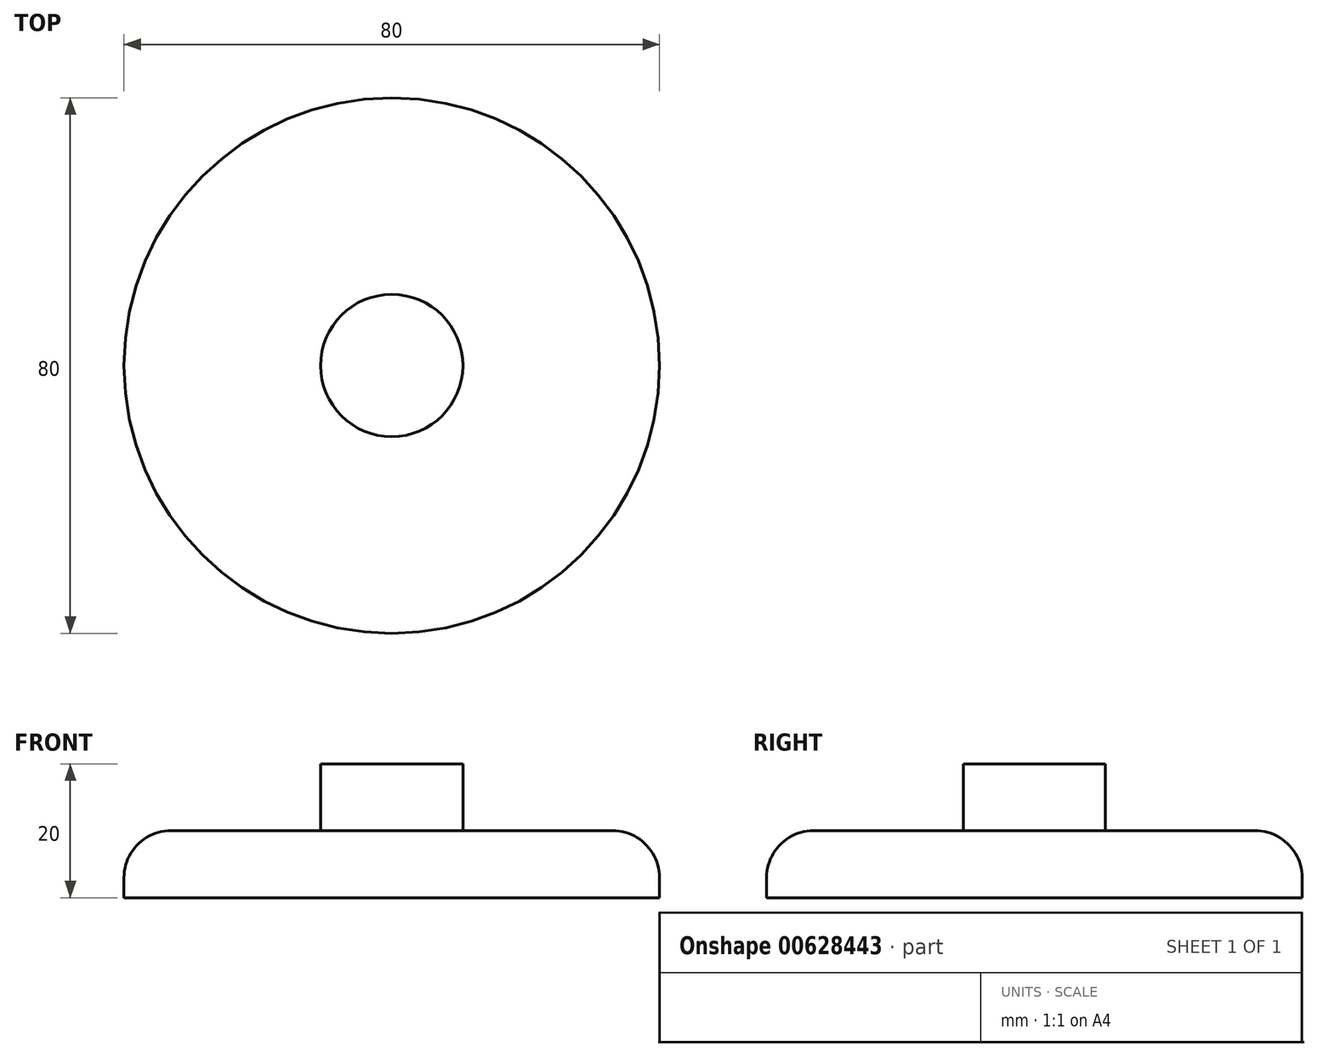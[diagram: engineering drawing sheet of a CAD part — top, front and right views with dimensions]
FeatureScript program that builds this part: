
annotation { "Feature Type Name" : "Feature", "Feature Type Description" : "" }
export const myFeature = defineFeature(function(context is Context, id is Id, definition is map)
    precondition{}
    {
        {
            var Q0;
            Q0=qCreatedBy(makeId("Top.planeOp"),FACE);
            var sketch = newSketch(context, id + "F0", { "sketchPlane" : qUnion([Q0])});
            skCircle(sketch, "E0", {"center": v(0, 0) * mm, "radius": 40 * mm});
            skSolve(sketch);
        }
        {
            var Q0;
            Q0 = qSketchRegion(id + "F0", true);
            extrude(context, id + "F1", {"entities" : qUnion([Q0]), "depth" : 10 * mm, "offsetDistance" : 25 * mm});
        }
        {
            var Q0;
            Q0=makeQuery(id+"F1.opExtrude","CAP_EDGE",EDGE,{"disambiguationData":[OSD([sQuery(id+"F0.wireOp",EDGE,"E0")])],"isStart":false});
            fillet(context, id + "F2", {"entities" : qUnion([Q0]), "radius" : 7 * mm, "tangentPropagation" : true, "allowEdgeOverflow" : false});
        }
        {
            var Q0;
            Q0=makeQuery(id+"F1.opExtrude","CAP_FACE",FACE,{"disambiguationData":[OSD([sQuery(id+"F0.wireOp",EDGE,"E0")])],"isStart":false});
            var sketch = newSketch(context, id + "F3", { "sketchPlane" : qUnion([Q0])});
            skCircle(sketch, "E1", {"center": v(0, 0) * mm, "radius": 10.62 * mm});
            skSolve(sketch);
        }
        {
            var Q0;
            Q0 = qSketchRegion(id + "F3", true);
            extrude(context, id + "F4", {"entities" : qUnion([Q0]), "operationType" : NewBodyOperationType.ADD, "depth" : 10 * mm, "offsetDistance" : 25 * mm});
        }
    });
